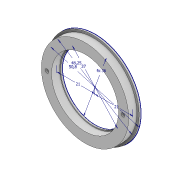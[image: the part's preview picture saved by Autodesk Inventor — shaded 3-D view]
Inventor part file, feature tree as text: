
AUTODESK INVENTOR PART (.ipt)
format: ipt  version: 2021 (Build 250183000, 183)  size: 114,688 bytes
history: native  units: mm
features: extrude x3, sketch x1, hole x1
ambient origin geometry x8: Origin, YZ Plane, XZ Plane, XY Plane, X Axis, Y Axis, Z Axis, Center Point
bodies: Solid1 (feature_tree)
feature tree (5):
  sketch  "Sketch1"  dims[d1=48.25mm d2=50.8mm d3=5.5mm d4=0.0mm d5=1.0mm d6=0.0mm d7=2.0mm d8=6.0mm d9=4.0mm d10=2.0mm d11=90.0deg d12=8.0mm d13=20.594885mm d14=21.0mm d15=21.0mm d16=36.0mm d17=1.0mm d18=0.0mm]
  extrude  "Extrusion1"  Depth=1.0mm
  extrude  "Extrusion2"  Depth=5.5mm TaperAngle=0.0deg
  hole  "Hole1"  [1 undecoded]
  extrude  "Extrusion3"  Depth=1.0mm
note: 1 required parameter value undecoded (feature->parameter linkage not recoverable at this tier; creation-order binding heuristic only, values carry confidence <= 0.55)
